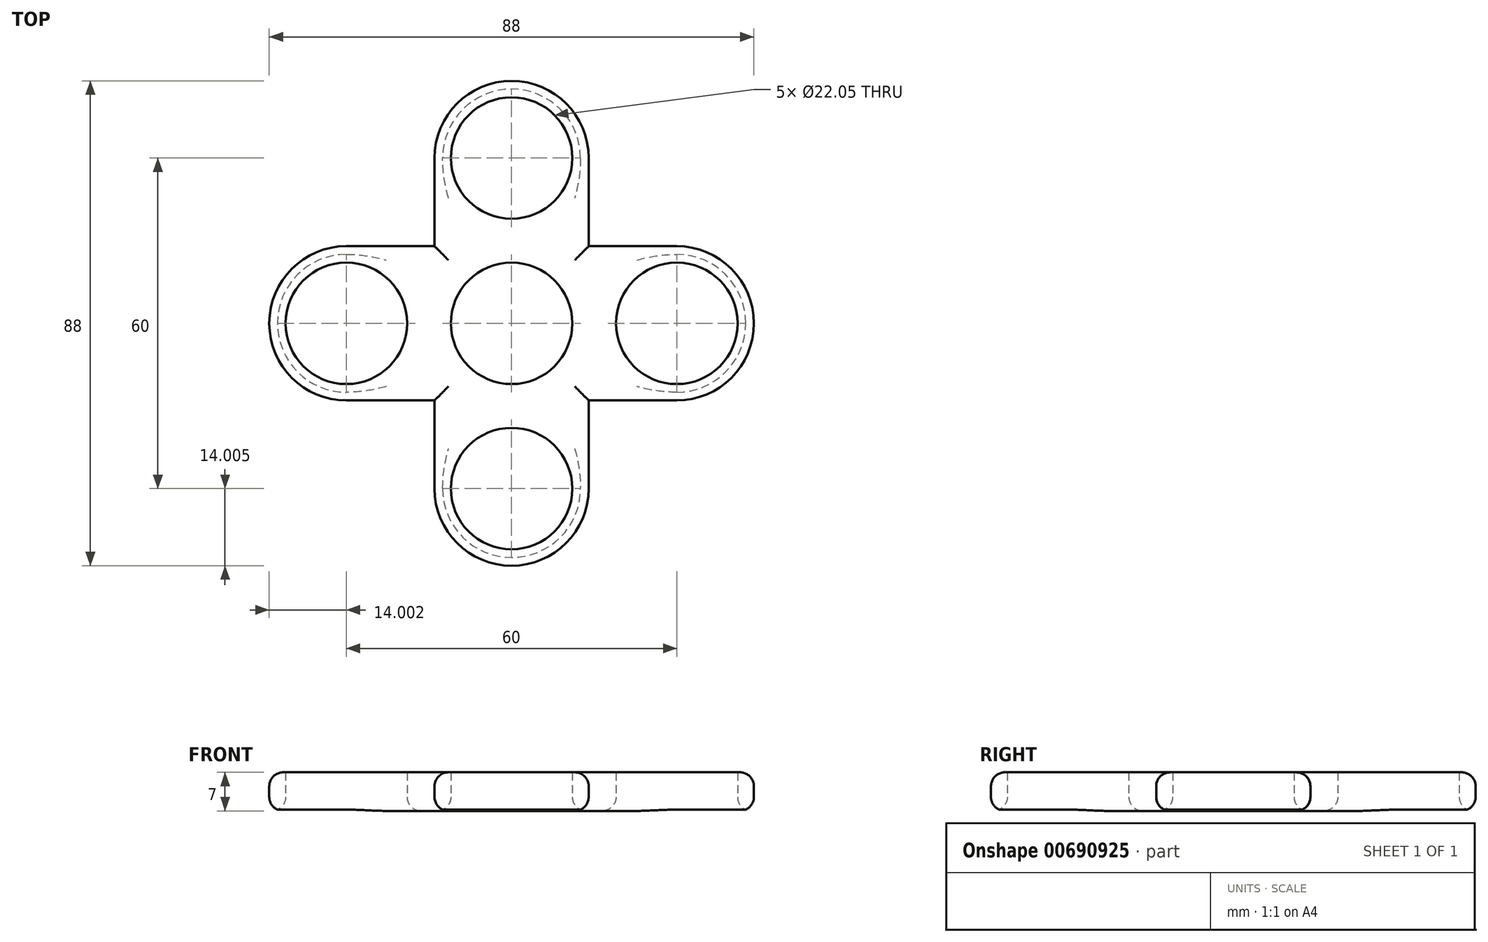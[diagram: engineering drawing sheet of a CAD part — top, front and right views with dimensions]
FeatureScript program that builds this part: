
annotation { "Feature Type Name" : "Feature", "Feature Type Description" : "" }
export const myFeature = defineFeature(function(context is Context, id is Id, definition is map)
    precondition{}
    {
        {
            var Q0;
            Q0=qCreatedBy(makeId("Top.planeOp"),FACE);
            var sketch = newSketch(context, id + "F0", { "sketchPlane" : qUnion([Q0])});
            skLineSegment(sketch, "E0.bottom", {"start": v(-5.05, 7.33) * mm, "end": v(22.95, 7.33) * mm});
            skLineSegment(sketch, "E0.top", {"start": v(-5.05, -22.67) * mm, "end": v(22.95, -22.67) * mm});
            skLineSegment(sketch, "E0.left", {"start": v(-5.05, 7.33) * mm, "end": v(-5.05, -22.67) * mm});
            skLineSegment(sketch, "E0.right", {"start": v(22.95, 7.33) * mm, "end": v(22.95, -22.67) * mm});
            skCircle(sketch, "E1", {"center": v(8.95, 7.33) * mm, "radius": 14 * mm});
            skCircle(sketch, "E2", {"center": v(8.95, 7.33) * mm, "radius": 11.03 * mm});
            skCircle(sketch, "E3", {"center": v(8.95, -22.67) * mm, "radius": 14 * mm});
            skCircle(sketch, "E4", {"center": v(8.95, -22.67) * mm, "radius": 11.03 * mm});
            skSolve(sketch);
        }
        {
            var Q0;
            Q0=qSketchRegion(id+"F0",true);
            extrude(context, id + "F1", {"entities" : qUnion([Q0]), "depth" : 7 * mm, "offsetDistance" : 25.4 * mm});
        }
        {
            var Q0;
            Q0=makeQuery(id+"F1.opExtrude","SWEPT_BODY",BODY,{"disambiguationData":[OSD([sQuery(id+"F0.wireOp",EDGE,"E0.left"),sQuery(id+"F0.wireOp",EDGE,"E0.right"),sQuery(id+"F0.wireOp",EDGE,"E1"),sQuery(id+"F0.wireOp",EDGE,"E2"),sQuery(id+"F0.wireOp",EDGE,"E3"),sQuery(id+"F0.wireOp",EDGE,"E4")])]});
            var Q1;
            Q1=makeQuery(id+"F1.opExtrude","SWEPT_FACE",FACE,{"disambiguationData":[OSD([sQuery(id+"F0.wireOp",EDGE,"E3")])]});
            circularPattern(context, id + "F2", {"entities" : qUnion([Q0]), "axis" : qUnion([Q1]), "angle" : 360 * degree, "instanceCount" : 4, "equalSpace" : true});
        }
        {
            var Q0;
            Q0=makeQuery(id+"F1.opExtrude","SWEPT_BODY",BODY,{"disambiguationData":[OSD([sQuery(id+"F0.wireOp",EDGE,"E0.left"),sQuery(id+"F0.wireOp",EDGE,"E0.right"),sQuery(id+"F0.wireOp",EDGE,"E1"),sQuery(id+"F0.wireOp",EDGE,"E2"),sQuery(id+"F0.wireOp",EDGE,"E3"),sQuery(id+"F0.wireOp",EDGE,"E4")])]});
            var Q1;
            Q1=makeQuery(id+"F2.opPattern","COPY",BODY,{"derivedFrom":makeQuery(id+"F1.opExtrude","SWEPT_BODY",BODY,{"disambiguationData":[OSD([sQuery(id+"F0.wireOp",EDGE,"E0.left"),sQuery(id+"F0.wireOp",EDGE,"E0.right"),sQuery(id+"F0.wireOp",EDGE,"E1"),sQuery(id+"F0.wireOp",EDGE,"E2"),sQuery(id+"F0.wireOp",EDGE,"E3"),sQuery(id+"F0.wireOp",EDGE,"E4")])]}),"instanceName":"1"});
            var Q2;
            Q2=makeQuery(id+"F2.opPattern","COPY",BODY,{"derivedFrom":makeQuery(id+"F1.opExtrude","SWEPT_BODY",BODY,{"disambiguationData":[OSD([sQuery(id+"F0.wireOp",EDGE,"E0.left"),sQuery(id+"F0.wireOp",EDGE,"E0.right"),sQuery(id+"F0.wireOp",EDGE,"E1"),sQuery(id+"F0.wireOp",EDGE,"E2"),sQuery(id+"F0.wireOp",EDGE,"E3"),sQuery(id+"F0.wireOp",EDGE,"E4")])]}),"instanceName":"2"});
            var Q3;
            Q3=makeQuery(id+"F2.opPattern","COPY",BODY,{"derivedFrom":makeQuery(id+"F1.opExtrude","SWEPT_BODY",BODY,{"disambiguationData":[OSD([sQuery(id+"F0.wireOp",EDGE,"E0.left"),sQuery(id+"F0.wireOp",EDGE,"E0.right"),sQuery(id+"F0.wireOp",EDGE,"E1"),sQuery(id+"F0.wireOp",EDGE,"E2"),sQuery(id+"F0.wireOp",EDGE,"E3"),sQuery(id+"F0.wireOp",EDGE,"E4")])]}),"instanceName":"3"});
            booleanBodies(context, id + "F3", {"operationType" : BooleanOperationType.UNION, "tools" : qUnion([Q0, Q1, Q2, Q3])});
        }
        {
            var Q0;
            Q0=makeQuery(id+"F2.opPattern","COPY",EDGE,{"derivedFrom":makeQuery(id+"F1.opExtrude","CAP_EDGE",EDGE,{"disambiguationData":[OSD([sQuery(id+"F0.wireOp",EDGE,"E1")])],"isStart":false}),"instanceName":"2"});
            var Q1;
            Q1=makeQuery(id+"F2.opPattern","COPY",EDGE,{"derivedFrom":makeQuery(id+"F1.opExtrude","CAP_EDGE",EDGE,{"disambiguationData":[OSD([sQuery(id+"F0.wireOp",EDGE,"E0.left")])],"isStart":false}),"instanceName":"2"});
            var Q2;
            Q2=makeQuery(id+"F2.opPattern","COPY",EDGE,{"derivedFrom":makeQuery(id+"F1.opExtrude","CAP_EDGE",EDGE,{"disambiguationData":[OSD([sQuery(id+"F0.wireOp",EDGE,"E0.right")])],"isStart":false}),"instanceName":"1"});
            var Q3;
            Q3=makeQuery(id+"F1.opExtrude","CAP_EDGE",EDGE,{"disambiguationData":[OSD([sQuery(id+"F0.wireOp",EDGE,"E1")])],"isStart":false});
            var Q4;
            Q4=makeQuery(id+"F1.opExtrude","CAP_EDGE",EDGE,{"disambiguationData":[OSD([sQuery(id+"F0.wireOp",EDGE,"E0.right")])],"isStart":false});
            var Q5;
            Q5=makeQuery(id+"F3.opBoolean","MERGE",EDGE,{"disambiguationData":[OD(1.0)],"derivedFrom":[makeQuery(id+"F2.opPattern","COPY",EDGE,{"derivedFrom":makeQuery(id+"F1.opExtrude","CAP_EDGE",EDGE,{"disambiguationData":[OSD([sQuery(id+"F0.wireOp",EDGE,"E0.left")])],"isStart":false}),"instanceName":"1"}),makeQuery(id+"F2.opPattern","COPY",EDGE,{"derivedFrom":makeQuery(id+"F1.opExtrude","CAP_EDGE",EDGE,{"disambiguationData":[OSD([sQuery(id+"F0.wireOp",EDGE,"E0.right")])],"isStart":false}),"instanceName":"3"})]});
            fillet(context, id + "F4", {"entities" : qUnion([Q0, Q1, Q2, Q3, Q4, Q5]), "radius" : 2.54 * mm, "tangentPropagation" : true, "allowEdgeOverflow" : false});
        }
        {
            var Q0;
            Q0=makeQuery(id+"F2.opPattern","COPY",EDGE,{"derivedFrom":makeQuery(id+"F1.opExtrude","CAP_EDGE",EDGE,{"disambiguationData":[OSD([sQuery(id+"F0.wireOp",EDGE,"E1")])],"isStart":true}),"instanceName":"1"});
            var Q1;
            Q1=makeQuery(id+"F1.opExtrude","CAP_EDGE",EDGE,{"disambiguationData":[OSD([sQuery(id+"F0.wireOp",EDGE,"E0.right")])],"isStart":true});
            var Q2;
            {var subQ0=makeQuery(id+"F1.opExtrude","CAP_FACE",FACE,{"disambiguationData":[OSD([sQuery(id+"F0.wireOp",EDGE,"E0.left"),sQuery(id+"F0.wireOp",EDGE,"E0.right"),sQuery(id+"F0.wireOp",EDGE,"E1"),sQuery(id+"F0.wireOp",EDGE,"E2"),sQuery(id+"F0.wireOp",EDGE,"E3"),sQuery(id+"F0.wireOp",EDGE,"E4")])],"isStart":true});Q2=makeQuery(id+"F3.opBoolean","MERGE",FACE,{"derivedFrom":[subQ0,makeQuery(id+"F2.opPattern","COPY",FACE,{"derivedFrom":subQ0,"instanceName":"1"}),makeQuery(id+"F2.opPattern","COPY",FACE,{"derivedFrom":subQ0,"instanceName":"2"}),makeQuery(id+"F2.opPattern","COPY",FACE,{"derivedFrom":subQ0,"instanceName":"3"})]});}
            fillet(context, id + "F5", {"entities" : qUnion([Q0, Q1, Q2]), "radius" : 2.54 * mm, "tangentPropagation" : true, "allowEdgeOverflow" : false});
        }
    });
